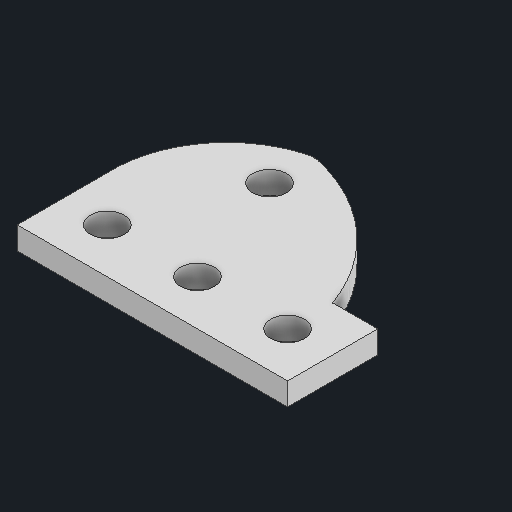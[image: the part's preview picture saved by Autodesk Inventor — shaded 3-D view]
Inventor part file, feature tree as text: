
AUTODESK INVENTOR PART (.ipt)
format: ipt  version: 2024 (Build 280153000, 153)  size: 117,248 bytes
history: native  units: in
note: dims shown in document units (in); Inventor stores cm internally (conversion verified against a paired STEP export)
features: other x3, sketch x1
ambient origin geometry x8: Origin, YZ Plane, XZ Plane, XY Plane, X Axis, Y Axis, Z Axis, Center Point
bodies: Solid1 (feature_tree)
feature tree (4):
  other  "wingpiece1.ipt"
  other  "Solid1::wingpiece1.ipt"
  other  "TaggingFeature1"
  sketch  "Sketch1"  dims[d0=0.3937in]
